# Revit family: L&L_LUCE&LIGHT_BRIGHT_9.7
name_source: partatom
category: Lighting Fixtures
revit_build: Autodesk Revit 2018 (Build: 20181011_1500(x64)
units: mm (PartAtom-declared; Revit-internal decimal feet)

## family parameters
Always vertical = Yes
Cut with Voids When Loaded = No
Host = Floor
Light Source = Yes
Part Type = Normal
Room Calculation Point = No
Round Connector Dimension = Use Diameter
Shared = No

## types (1)
- L&L_LUCE&LIGHT_BRIGHT_9.7
    ACCESSORIES = Outer casing
    BIM BADGE = https://bim.archiproducts.com
    BODY MATERIAL = ANODIZED ALUMINIUM
    Color Filter = 16777215
    DIAMETER = 130 mm  [stored 0.426509 ft]
    Description = Recessed for outdoor applications
    Dimming Lamp Color Temperature Shift = <None>
    ENERGY EFFIECIENCY CLASS = A / A+ / A++
    Emit Shape Visible in Rendering = No
    Emit from Circle Diameter = 610 mm
    HEIGHT = 47 mm  [stored 0.154199 ft]
    ILLUMINITECHNICAL PERFORMANCE = 3000K - 4W - 24Vdc
    Lamp = LED colour white: 2700K, 3000K, 4000K
    MATERIAL DESCRIPTION = Body: anodized aluminium; Trim: stainless steel; Screen: PMMA plastic
    Manufacturer = L&L Luce&light
    Model = BRIGHT 9.7
    PHOTOMETRIC CURVE = BRIGHT 9.7 R [3000K 4W 24Vdc]
    POWER CONSUMPTION = 4 W
    POWER SUPPLY = 24 Vdc
    PRODUCT CODE CONFIGURATOR = https://www.lucelight.it
    PROTECTION LEVEL = IP 68
    Photometric Web File = BRIGHT 9.7 R [3000K 4W 24Vdc].IES
    SCREEN MATERIAL = PMMA PLASTIC
    TECHNICAL SHEET = https://www.lucelight.it
    TRIM MATERIAL = AISI 316L STAINLESS STEEL
    Tilt Angle = -90.00°
    Type Comments = Recessed (floor)
    URL = https://www.lucelight.it
    URL ACCESSORIES DXF = https://www.lucelight.it
    URL ACCESSORIES DXF 2 = https://www.lucelight.it
    URL ACCESSORIES DXF 3 = https://www.lucelight.it
    URL CATALOGUE = https://www.lucelight.it
    URL DESCRIPTION = https://www.lucelight.it
    URL DXF = https://www.lucelight.it
    URL IMAGE = https://www.lucelight.it
    WEIGHT KG = 1.21

note: [stored X ft] marks values corroborated as IEEE doubles in the binary element streams (Revit-internal decimal feet)

## geometry (parser evidence)
native form markers: Blend x6, Sweep x2
no freeform markers — native parametric forms only
